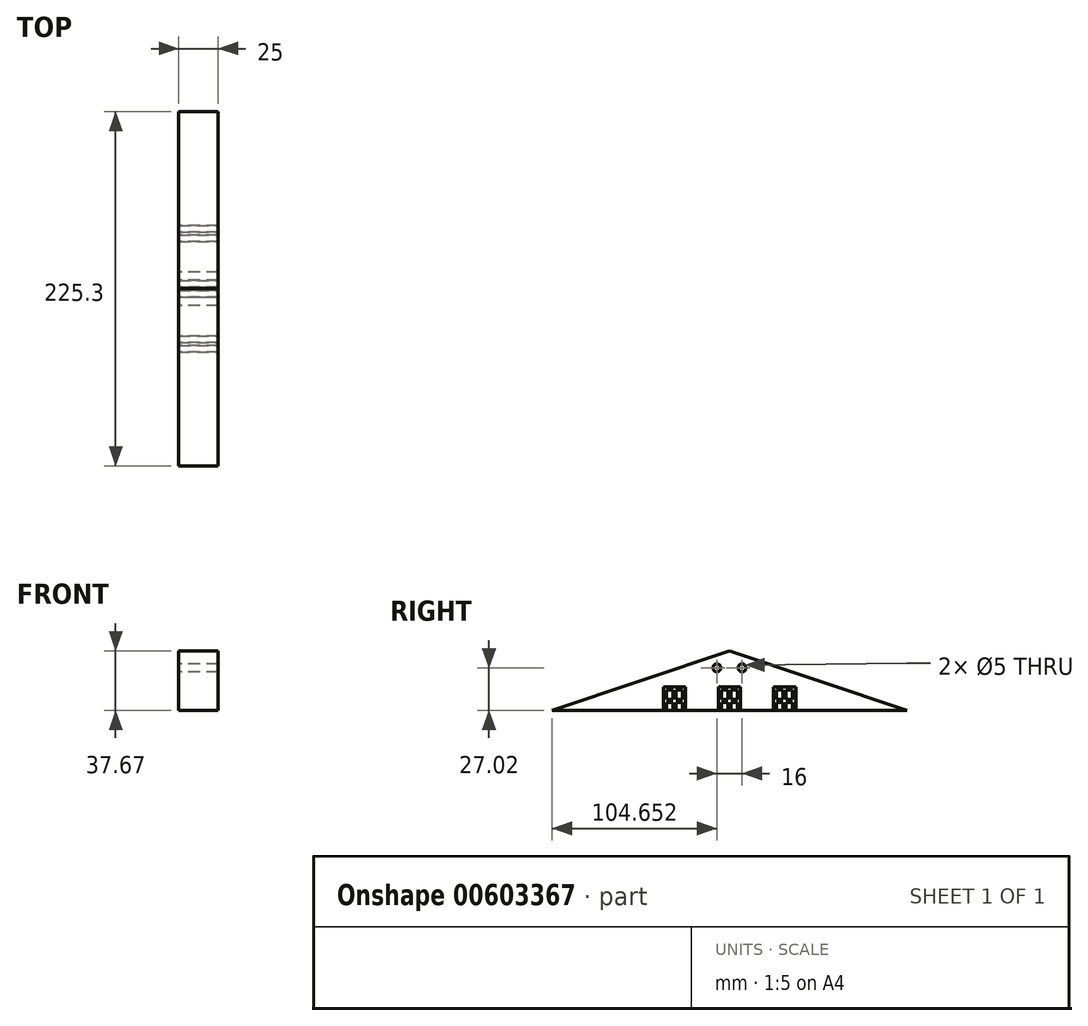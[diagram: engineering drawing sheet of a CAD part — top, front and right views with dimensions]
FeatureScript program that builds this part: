
annotation { "Feature Type Name" : "Feature", "Feature Type Description" : "" }
export const myFeature = defineFeature(function(context is Context, id is Id, definition is map)
    precondition{}
    {
        {
            var Q0;
            Q0=qCreatedBy(makeId("Top.planeOp"),FACE);
            var sketch = newSketch(context, id + "F0", { "sketchPlane" : qUnion([Q0])});
            skLineSegment(sketch, "E0", {"start": v(-327.3, -140.86) * mm, "end": v(-102.6, -140.86) * mm});
            skLineSegment(sketch, "E1", {"start": v(-102.6, -140.86) * mm, "end": v(-102.6, -170.86) * mm});
            skLineSegment(sketch, "E2", {"start": v(-102.6, -170.86) * mm, "end": v(0, -170.86) * mm});
            skLineSegment(sketch, "E3", {"start": v(0, -170.86) * mm, "end": v(0, -140.86) * mm});
            skLineSegment(sketch, "E4", {"start": v(0, -140.86) * mm, "end": v(288.9, -140.86) * mm});
            skLineSegment(sketch, "E5", {"start": v(288.9, -140.86) * mm, "end": v(288.9, 108.14) * mm});
            skLineSegment(sketch, "E6", {"start": v(288.9, 108.14) * mm, "end": v(0, 108.14) * mm});
            skLineSegment(sketch, "E7", {"start": v(0, 108.14) * mm, "end": v(0, 138.14) * mm});
            skLineSegment(sketch, "E8", {"start": v(-102.6, 128.64) * mm, "end": v(-102.6, 108.14) * mm});
            skLineSegment(sketch, "E9", {"start": v(-102.6, 108.14) * mm, "end": v(-327.3, 108.14) * mm});
            skLineSegment(sketch, "E10", {"start": v(-327.3, 108.14) * mm, "end": v(-327.3, -140.86) * mm});
            skLineSegment(sketch, "E11", {"start": v(-102.6, 128.64) * mm, "end": v(0, 138.14) * mm});
            skSolve(sketch);
        }
        {
            var Q0;
            Q0=makeQuery(id+"F0.imprint","IMPRINT",FACE,{"disambiguationData":[TD([[makeQuery(id+"F0.imprint","IMPRINT",EDGE,{"derivedFrom":sQuery(id+"F0.wireOp",EDGE,"E0")}),1.0]])]});
            extrude(context, id + "F1", {"entities" : qUnion([Q0]), "depth" : 8 * mm, "offsetDistance" : 25 * mm});
        }
        {
            var Q0;
            Q0=makeQuery(id+"F1.opExtrude","SWEPT_FACE",FACE,{"disambiguationData":[OSD([sQuery(id+"F0.wireOp",EDGE,"E5")])]});
            var sketch = newSketch(context, id + "F2", { "sketchPlane" : qUnion([Q0])});
            skLineSegment(sketch, "E12", {"start": v(-146.36, 8) * mm, "end": v(113.64, 8) * mm});
            skPoint(sketch, "E13", {"position": v(-140.86, 8) * mm});
            skPoint(sketch, "E14", {"position": v(108.14, 8) * mm});
            skLineSegment(sketch, "E15", {"start": v(-146.36, 8) * mm, "end": v(-16.36, 51.45) * mm});
            skLineSegment(sketch, "E16", {"start": v(-16.36, 51.45) * mm, "end": v(113.64, 8) * mm});
            skPoint(sketch, "E17", {"position": v(-16.36, 8) * mm});
            skSolve(sketch);
        }
        {
            var Q0;
            {var subQ0=sQuery(id+"F2.wireOp",EDGE,"E15");Q0=makeQuery(id+"F2.imprint","IMPRINT",FACE,{"disambiguationData":[TD([[makeQuery(id+"F2.imprint","IMPRINT",EDGE,{"derivedFrom":subQ0}),-1.0]])]});}
            extrude(context, id + "F3", {"entities" : qUnion([Q0]), "operationType" : NewBodyOperationType.ADD, "oppositeDirection" : true, "depth" : (616.2 + 5.5) * mm, "offsetDistance" : 25 * mm});
        }
        {
            var Q0;
            Q0=qSketchRegion(id+"F2",true);
            extrude(context, id + "F4", {"entities" : qUnion([Q0]), "operationType" : NewBodyOperationType.ADD, "depth" : 5.5 * mm, "offsetDistance" : 25 * mm});
        }
        {
            var Q0;
            Q0=makeQuery(id+"F1.opExtrude","SWEPT_FACE",FACE,{"disambiguationData":[OSD([sQuery(id+"F0.wireOp",EDGE,"E2")])]});
            var sketch = newSketch(context, id + "F5", { "sketchPlane" : qUnion([Q0])});
            skLineSegment(sketch, "E18", {"start": v(-108.1, 8) * mm, "end": v(5.5, 8) * mm});
            skPoint(sketch, "E19", {"position": v(-102.6, 8) * mm});
            skPoint(sketch, "E20", {"position": v(0, 8) * mm});
            skPoint(sketch, "E21", {"position": v(-51.3, 8) * mm});
            skLineSegment(sketch, "E22", {"start": v(-51.3, 8) * mm, "end": v(-51.3, 90.85) * mm, "construction": true});
            skPoint(sketch, "E23", {"position": v(-51.3, 62.75) * mm});
            skLineSegment(sketch, "E24", {"start": v(-108.1, 8) * mm, "end": v(-51.3, 62.75) * mm});
            skLineSegment(sketch, "E25", {"start": v(-51.3, 62.75) * mm, "end": v(5.5, 8) * mm});
            skSolve(sketch);
        }
        {
            var Q0;
            Q0=qSketchRegion(id+"F5",true);
            var Q1;
            Q1=makeQuery(id+"F1.opExtrude","SWEPT_FACE",FACE,{"disambiguationData":[OSD([sQuery(id+"F0.wireOp",EDGE,"E11")])]});
            extrude(context, id + "F6", {"entities" : qUnion([Q0]), "operationType" : NewBodyOperationType.ADD, "endBound" : BoundingType.UP_TO_SURFACE, "oppositeDirection" : true, "depth" : 25 * mm, "endBoundEntityFace" : qUnion([Q1]), "hasOffset" : true, "offsetDistance" : -5.5 * mm});
        }
        {
            var Q0;
            Q0=qSketchRegion(id+"F5",true);
            extrude(context, id + "F7", {"entities" : qUnion([Q0]), "operationType" : NewBodyOperationType.ADD, "depth" : 5.5 * mm, "offsetDistance" : 25 * mm});
        }
        {
            var Q0;
            Q0=makeQuery(id+"F6.opExtrude","CAP_FACE",FACE,{"disambiguationData":[OSD([sQuery(id+"F5.wireOp",EDGE,"E18"),sQuery(id+"F5.wireOp",EDGE,"E24"),sQuery(id+"F5.wireOp",EDGE,"E25")])],"isStart":false});
            var sketch = newSketch(context, id + "F8", { "sketchPlane" : qUnion([Q0])});
            skLineSegment(sketch, "E26.0", {"start": v(38.28, 55.82) * mm, "end": v(-15.3, 4.4) * mm});
            skLineSegment(sketch, "E26.1", {"start": v(91.86, 4.4) * mm, "end": v(38.28, 55.82) * mm});
            skLineSegment(sketch, "E27", {"start": v(-15.3, 4.4) * mm, "end": v(91.86, 4.4) * mm});
            skSolve(sketch);
        }
        {
            var Q0;
            {var subQ0=sQuery(id+"F8.wireOp",EDGE,"E26.1");var subQ1=sQuery(id+"F8.wireOp",EDGE,"E26.0");var subQ2=makeQuery(id+"F8.imprint","INTERSECT",VERTEX,{"derivedFrom":[subQ1,subQ0]});Q0=makeQuery(id+"F8.imprint","IMPRINT",FACE,{"disambiguationData":[TD([[makeQuery(id+"F8.imprint","IMPRINT",EDGE,{"disambiguationData":[TD([[subQ2,-1.0]])],"derivedFrom":subQ1}),1.0]])]});}
            extrude(context, id + "F9", {"entities" : qUnion([Q0]), "operationType" : NewBodyOperationType.REMOVE, "oppositeDirection" : true, "depth" : 5.5 * mm, "offsetDistance" : 25 * mm});
        }
        {
            var Q0;
            Q0=makeQuery(id+"F3.opExtrude","CAP_FACE",FACE,{"disambiguationData":[OSD([sQuery(id+"F2.wireOp",EDGE,"E12"),sQuery(id+"F2.wireOp",EDGE,"E15"),sQuery(id+"F2.wireOp",EDGE,"E16")])],"isStart":false});
            var sketch = newSketch(context, id + "F10", { "sketchPlane" : qUnion([Q0])});
            skLineSegment(sketch, "E28.0", {"start": v(16.36, 45.65) * mm, "end": v(-111.9, 2.78) * mm});
            skLineSegment(sketch, "E28.1", {"start": v(144.61, 2.78) * mm, "end": v(16.36, 45.65) * mm});
            skLineSegment(sketch, "E29", {"start": v(-111.9, 2.78) * mm, "end": v(144.61, 2.78) * mm});
            skSolve(sketch);
        }
        {
            var Q0;
            Q0=qSketchRegion(id+"F10",true);
            extrude(context, id + "F11", {"entities" : qUnion([Q0]), "operationType" : NewBodyOperationType.REMOVE, "oppositeDirection" : true, "depth" : 5.5 * mm, "offsetDistance" : 25 * mm});
        }
        {
            var Q0;
            Q0=makeQuery(id+"F4.opExtrude","CAP_FACE",FACE,{"disambiguationData":[OSD([sQuery(id+"F2.wireOp",EDGE,"E12"),sQuery(id+"F2.wireOp",EDGE,"E15"),sQuery(id+"F2.wireOp",EDGE,"E16")])],"isStart":false});
            var sketch = newSketch(context, id + "F12", { "sketchPlane" : qUnion([Q0])});
            skLineSegment(sketch, "E30.0", {"start": v(-16.36, 45.65) * mm, "end": v(111.9, 2.78) * mm});
            skLineSegment(sketch, "E30.1", {"start": v(-144.61, 2.78) * mm, "end": v(-16.36, 45.65) * mm});
            skLineSegment(sketch, "E31", {"start": v(-144.61, 2.78) * mm, "end": v(111.9, 2.78) * mm});
            skSolve(sketch);
        }
        {
            var Q0;
            Q0=qSketchRegion(id+"F12",true);
            extrude(context, id + "F13", {"entities" : qUnion([Q0]), "operationType" : NewBodyOperationType.REMOVE, "oppositeDirection" : true, "depth" : 5.5 * mm, "offsetDistance" : 25 * mm});
        }
        {
            var Q0;
            Q0=makeQuery(id+"F7.opExtrude","CAP_FACE",FACE,{"disambiguationData":[OSD([sQuery(id+"F5.wireOp",EDGE,"E18"),sQuery(id+"F5.wireOp",EDGE,"E24"),sQuery(id+"F5.wireOp",EDGE,"E25")])],"isStart":false});
            var sketch = newSketch(context, id + "F14", { "sketchPlane" : qUnion([Q0])});
            skLineSegment(sketch, "E32.0", {"start": v(-51.3, 55.11) * mm, "end": v(1.68, 4.04) * mm});
            skLineSegment(sketch, "E32.1", {"start": v(-104.28, 4.04) * mm, "end": v(-51.3, 55.11) * mm});
            skLineSegment(sketch, "E33", {"start": v(-104.28, 4.04) * mm, "end": v(1.68, 4.04) * mm});
            skSolve(sketch);
        }
        {
            var Q0;
            Q0=qSketchRegion(id+"F14",true);
            extrude(context, id + "F15", {"entities" : qUnion([Q0]), "operationType" : NewBodyOperationType.REMOVE, "oppositeDirection" : true, "depth" : 5.5 * mm, "offsetDistance" : 25 * mm});
        }
        {
            var Q0;
            Q0=makeQuery(id+"F4.opExtrude","CAP_FACE",FACE,{"disambiguationData":[OSD([sQuery(id+"F2.wireOp",EDGE,"E12"),sQuery(id+"F2.wireOp",EDGE,"E15"),sQuery(id+"F2.wireOp",EDGE,"E16")])],"isStart":false});
            var sketch = newSketch(context, id + "F16", { "sketchPlane" : qUnion([Q0])});
            skLineSegment(sketch, "E34", {"start": v(-36.64, 44.67) * mm, "end": v(-16.36, 51.45) * mm});
            skLineSegment(sketch, "E35", {"start": v(-16.36, 51.45) * mm, "end": v(3.93, 44.67) * mm});
            skLineSegment(sketch, "E36.0", {"start": v(-16.36, 55.67) * mm, "end": v(5.2, 48.47) * mm});
            skLineSegment(sketch, "E36.1", {"start": v(-37.91, 48.47) * mm, "end": v(-16.36, 55.67) * mm});
            skLineSegment(sketch, "E37", {"start": v(-37.91, 48.47) * mm, "end": v(-36.64, 44.67) * mm});
            skLineSegment(sketch, "E38", {"start": v(5.2, 48.47) * mm, "end": v(3.93, 44.67) * mm});
            skSolve(sketch);
        }
        {
            var Q0;
            Q0=makeQuery(id+"F16.imprint","IMPRINT",FACE,{"disambiguationData":[TD([[makeQuery(id+"F16.imprint","IMPRINT",EDGE,{"derivedFrom":sQuery(id+"F16.wireOp",EDGE,"E34")}),1.0]])]});
            extrude(context, id + "F17", {"entities" : qUnion([Q0]), "operationType" : NewBodyOperationType.ADD, "oppositeDirection" : true, "depth" : (30.35 + 277.85) * mm, "offsetDistance" : 25 * mm});
        }
        {
            var Q0;
            Q0=qSketchRegion(id+"F16",true);
            extrude(context, id + "F18", {"entities" : qUnion([Q0]), "operationType" : NewBodyOperationType.REMOVE, "oppositeDirection" : true, "depth" : 24 * mm, "offsetDistance" : 25 * mm});
        }
        {
            var Q0;
            Q0=makeQuery(id+"F3.opExtrude","CAP_FACE",FACE,{"disambiguationData":[OSD([sQuery(id+"F2.wireOp",EDGE,"E12"),sQuery(id+"F2.wireOp",EDGE,"E15"),sQuery(id+"F2.wireOp",EDGE,"E16")])],"isStart":false});
            var sketch = newSketch(context, id + "F19", { "sketchPlane" : qUnion([Q0])});
            skLineSegment(sketch, "E39", {"start": v(-3.93, 44.67) * mm, "end": v(16.36, 51.45) * mm});
            skLineSegment(sketch, "E40", {"start": v(16.36, 51.45) * mm, "end": v(36.64, 44.67) * mm});
            skLineSegment(sketch, "E41.0", {"start": v(16.36, 55.67) * mm, "end": v(37.91, 48.47) * mm});
            skLineSegment(sketch, "E41.1", {"start": v(-5.2, 48.47) * mm, "end": v(16.36, 55.67) * mm});
            skLineSegment(sketch, "E42", {"start": v(-5.2, 48.47) * mm, "end": v(-3.93, 44.67) * mm});
            skLineSegment(sketch, "E43", {"start": v(37.91, 48.47) * mm, "end": v(36.64, 44.67) * mm});
            skSolve(sketch);
        }
        {
            var Q0;
            Q0=qSketchRegion(id+"F19",true);
            extrude(context, id + "F20", {"entities" : qUnion([Q0]), "operationType" : NewBodyOperationType.ADD, "oppositeDirection" : true, "depth" : (30.35 + 213.85) * mm, "offsetDistance" : 25 * mm});
        }
        {
            var Q0;
            Q0=qSketchRegion(id+"F19",true);
            extrude(context, id + "F21", {"entities" : qUnion([Q0]), "operationType" : NewBodyOperationType.REMOVE, "oppositeDirection" : true, "depth" : 30.35 * mm, "offsetDistance" : 25 * mm});
        }
        {
            var Q0;
            Q0=makeQuery(id+"F11.boolean.opBoolean","MERGE",FACE,{"derivedFrom":[makeQuery(id+"F1.opExtrude","SWEPT_FACE",FACE,{"disambiguationData":[OSD([sQuery(id+"F0.wireOp",EDGE,"E10")])]}),makeQuery(id+"F11.opExtrude","CAP_FACE",FACE,{"disambiguationData":[OSD([sQuery(id+"F10.wireOp",EDGE,"E28.0"),sQuery(id+"F10.wireOp",EDGE,"E28.1"),sQuery(id+"F10.wireOp",EDGE,"E29")])],"isStart":false})]});
            var sketch = newSketch(context, id + "F22", { "sketchPlane" : qUnion([Q0])});
            skPoint(sketch, "E44", {"position": v(16.36, 0) * mm});
            skLineSegment(sketch, "E45", {"start": v(16.36, 0) * mm, "end": v(16.36, 35) * mm, "construction": true});
            skLineSegment(sketch, "E46", {"start": v(-4.2, 35) * mm, "end": v(35.76, 35) * mm, "construction": true});
            skPoint(sketch, "E47", {"position": v(8.36, 35) * mm});
            skPoint(sketch, "E48", {"position": v(24.36, 35) * mm});
            skCircle(sketch, "E49", {"center": v(8.36, 35) * mm, "radius": 2.5 * mm});
            skCircle(sketch, "E50", {"center": v(24.36, 35) * mm, "radius": 2.5 * mm});
            skSolve(sketch);
        }
        {
            var Q0;
            Q0=qSketchRegion(id+"F22",true);
            extrude(context, id + "F23", {"entities" : qUnion([Q0]), "operationType" : NewBodyOperationType.REMOVE, "oppositeDirection" : true, "depth" : .5 * mm, "offsetDistance" : 25 * mm});
        }
        {
            var Q0;
            Q0=makeQuery(id+"F13.boolean.opBoolean","MERGE",FACE,{"derivedFrom":[makeQuery(id+"F3.boolean.opBoolean","MERGE",FACE,{"derivedFrom":[makeQuery(id+"F1.opExtrude","SWEPT_FACE",FACE,{"disambiguationData":[OSD([sQuery(id+"F0.wireOp",EDGE,"E5")])]}),makeQuery(id+"F3.opExtrude","CAP_FACE",FACE,{"disambiguationData":[OSD([sQuery(id+"F2.wireOp",EDGE,"E12"),sQuery(id+"F2.wireOp",EDGE,"E15"),sQuery(id+"F2.wireOp",EDGE,"E16")])],"isStart":true})]}),makeQuery(id+"F13.opExtrude","CAP_FACE",FACE,{"disambiguationData":[OSD([sQuery(id+"F12.wireOp",EDGE,"E30.0"),sQuery(id+"F12.wireOp",EDGE,"E30.1"),sQuery(id+"F12.wireOp",EDGE,"E31")])],"isStart":false})]});
            var sketch = newSketch(context, id + "F24", { "sketchPlane" : qUnion([Q0])});
            skPoint(sketch, "E51", {"position": v(-16.36, 0) * mm});
            skLineSegment(sketch, "E52", {"start": v(-16.36, 0) * mm, "end": v(-16.36, 35) * mm, "construction": true});
            skLineSegment(sketch, "E53", {"start": v(-48.45, 35) * mm, "end": v(-8.49, 35) * mm, "construction": true});
            skPoint(sketch, "E54", {"position": v(-24.36, 35) * mm});
            skPoint(sketch, "E55", {"position": v(-8.36, 35) * mm});
            skCircle(sketch, "E56", {"center": v(-24.36, 35) * mm, "radius": 2.5 * mm});
            skCircle(sketch, "E57", {"center": v(-8.36, 35) * mm, "radius": 2.5 * mm});
            skSolve(sketch);
        }
        {
            var Q0;
            Q0=qSketchRegion(id+"F24",true);
            extrude(context, id + "F25", {"entities" : qUnion([Q0]), "operationType" : NewBodyOperationType.REMOVE, "oppositeDirection" : true, "depth" : .5 * mm, "offsetDistance" : 25 * mm});
        }
        {
            var Q0;
            Q0=makeQuery(id+"F15.boolean.opBoolean","MERGE",FACE,{"derivedFrom":[makeQuery(id+"F6.boolean.opBoolean","MERGE",FACE,{"derivedFrom":[makeQuery(id+"F1.opExtrude","SWEPT_FACE",FACE,{"disambiguationData":[OSD([sQuery(id+"F0.wireOp",EDGE,"E2")])]}),makeQuery(id+"F6.opExtrude","CAP_FACE",FACE,{"disambiguationData":[OSD([sQuery(id+"F5.wireOp",EDGE,"E18"),sQuery(id+"F5.wireOp",EDGE,"E24"),sQuery(id+"F5.wireOp",EDGE,"E25")])],"isStart":true})]})],"fromTools":[makeQuery(id+"F15.opExtrude","CAP_FACE",FACE,{"disambiguationData":[OSD([sQuery(id+"F14.wireOp",EDGE,"E32.0"),sQuery(id+"F14.wireOp",EDGE,"E32.1"),sQuery(id+"F14.wireOp",EDGE,"E33")])],"isStart":false})]});
            var sketch = newSketch(context, id + "F26", { "sketchPlane" : qUnion([Q0])});
            skPoint(sketch, "E58", {"position": v(-51.3, 0) * mm});
            skLineSegment(sketch, "E59", {"start": v(-51.3, 0) * mm, "end": v(-51.3, 35) * mm, "construction": true});
            skLineSegment(sketch, "E60", {"start": v(-73.66, 35) * mm, "end": v(-33.7, 35) * mm, "construction": true});
            skPoint(sketch, "E61", {"position": v(-59.3, 35) * mm});
            skPoint(sketch, "E62", {"position": v(-43.3, 35) * mm});
            skCircle(sketch, "E63", {"center": v(-59.3, 35) * mm, "radius": 2.5 * mm});
            skCircle(sketch, "E64", {"center": v(-43.3, 35) * mm, "radius": 2.5 * mm});
            skSolve(sketch);
        }
        {
            var Q0;
            Q0=qSketchRegion(id+"F26",true);
            extrude(context, id + "F27", {"entities" : qUnion([Q0]), "operationType" : NewBodyOperationType.REMOVE, "oppositeDirection" : true, "depth" : .5 * mm, "offsetDistance" : 25 * mm});
        }
        {
            var Q0;
            Q0=makeQuery(id+"F1.opExtrude","SWEPT_FACE",FACE,{"disambiguationData":[OSD([sQuery(id+"F0.wireOp",EDGE,"E11")])]});
            var sketch = newSketch(context, id + "F28", { "sketchPlane" : qUnion([Q0])});
            skPoint(sketch, "E65", {"position": v(38.78, 0) * mm});
            skLineSegment(sketch, "E66", {"start": v(38.78, 0) * mm, "end": v(38.78, 35) * mm, "construction": true});
            skLineSegment(sketch, "E67", {"start": v(13.04, 35) * mm, "end": v(53, 35) * mm, "construction": true});
            skPoint(sketch, "E68", {"position": v(30.78, 35) * mm});
            skPoint(sketch, "E69", {"position": v(46.78, 35) * mm});
            skCircle(sketch, "E70", {"center": v(30.78, 35) * mm, "radius": 2.5 * mm});
            skCircle(sketch, "E71", {"center": v(46.78, 35) * mm, "radius": 2.5 * mm});
            skSolve(sketch);
        }
        {
            var Q0;
            Q0=qSketchRegion(id+"F28",true);
            extrude(context, id + "F29", {"entities" : qUnion([Q0]), "operationType" : NewBodyOperationType.REMOVE, "oppositeDirection" : true, "depth" : .5 * mm, "offsetDistance" : 25 * mm});
        }
        {
            var Q0;
            Q0=makeQuery(id+"F13.boolean.opBoolean","MERGE",FACE,{"derivedFrom":[makeQuery(id+"F3.boolean.opBoolean","MERGE",FACE,{"derivedFrom":[makeQuery(id+"F1.opExtrude","SWEPT_FACE",FACE,{"disambiguationData":[OSD([sQuery(id+"F0.wireOp",EDGE,"E5")])]}),makeQuery(id+"F3.opExtrude","CAP_FACE",FACE,{"disambiguationData":[OSD([sQuery(id+"F2.wireOp",EDGE,"E12"),sQuery(id+"F2.wireOp",EDGE,"E15"),sQuery(id+"F2.wireOp",EDGE,"E16")])],"isStart":true})]}),makeQuery(id+"F13.opExtrude","CAP_FACE",FACE,{"disambiguationData":[OSD([sQuery(id+"F12.wireOp",EDGE,"E30.0"),sQuery(id+"F12.wireOp",EDGE,"E30.1"),sQuery(id+"F12.wireOp",EDGE,"E31")])],"isStart":false})]});
            var sketch = newSketch(context, id + "F30", { "sketchPlane" : qUnion([Q0])});
            skPoint(sketch, "E72", {"position": v(-16.36, 0) * mm});
            skLineSegment(sketch, "E73", {"start": v(-16.36, 0) * mm, "end": v(-16.36, 40.85) * mm, "construction": true});
            skLineSegment(sketch, "E74.bottom", {"start": v(-23.43, 23) * mm, "end": v(-9.29, 23) * mm});
            skLineSegment(sketch, "E74.top", {"start": v(-23.43, 5) * mm, "end": v(-9.29, 5) * mm});
            skLineSegment(sketch, "E74.left", {"start": v(-23.43, 23) * mm, "end": v(-23.43, 5) * mm});
            skLineSegment(sketch, "E74.right", {"start": v(-9.29, 23) * mm, "end": v(-9.29, 5) * mm});
            skLineSegment(sketch, "E75.0", {"start": v(-21.5, 21.07) * mm, "end": v(-17.32, 21.07) * mm});
            skLineSegment(sketch, "E75.1", {"start": v(-21.5, 21.07) * mm, "end": v(-21.5, 14.96) * mm});
            skLineSegment(sketch, "E75.2", {"start": v(-21.5, 6.93) * mm, "end": v(-17.32, 6.93) * mm});
            skLineSegment(sketch, "E75.3", {"start": v(-11.21, 21.07) * mm, "end": v(-11.21, 14.96) * mm});
            skLineSegment(sketch, "E76.left", {"start": v(-17.32, 21.07) * mm, "end": v(-17.32, 14.96) * mm});
            skLineSegment(sketch, "E76.right", {"start": v(-15.4, 21.07) * mm, "end": v(-15.4, 14.96) * mm});
            skLineSegment(sketch, "E77.bottom", {"start": v(-11.21, 14.96) * mm, "end": v(-15.4, 14.96) * mm});
            skLineSegment(sketch, "E77.top", {"start": v(-11.21, 13.04) * mm, "end": v(-15.4, 13.04) * mm});
            skLineSegment(sketch, "E78.trimOffspring", {"start": v(-17.32, 14.96) * mm, "end": v(-21.5, 14.96) * mm});
            skLineSegment(sketch, "E79.trimOffspring", {"start": v(-17.32, 13.04) * mm, "end": v(-17.32, 6.93) * mm});
            skLineSegment(sketch, "E80.trimOffspring", {"start": v(-17.32, 13.04) * mm, "end": v(-21.5, 13.04) * mm});
            skLineSegment(sketch, "E81.trimOffspring", {"start": v(-15.4, 13.04) * mm, "end": v(-15.4, 6.93) * mm});
            skLineSegment(sketch, "E82.trimOffspring", {"start": v(-11.21, 13.04) * mm, "end": v(-11.21, 6.93) * mm});
            skLineSegment(sketch, "E83.trimOffspring", {"start": v(-21.5, 13.04) * mm, "end": v(-21.5, 6.93) * mm});
            skLineSegment(sketch, "E84.trimOffspring", {"start": v(-15.4, 21.07) * mm, "end": v(-11.21, 21.07) * mm});
            skLineSegment(sketch, "E85.trimOffspring", {"start": v(-15.4, 6.93) * mm, "end": v(-11.21, 6.93) * mm});
            skPoint(sketch, "E86", {"position": v(-16.36, 23) * mm});
            skLineSegment(sketch, "E87.1.0.0", {"start": v(19.6, 13.04) * mm, "end": v(19.6, 6.93) * mm});
            skPoint(sketch, "E87.1.0.1", {"position": v(18.64, 23) * mm});
            skLineSegment(sketch, "E87.1.0.2", {"start": v(19.6, 6.93) * mm, "end": v(23.79, 6.93) * mm});
            skLineSegment(sketch, "E87.1.0.3", {"start": v(13.5, 13.04) * mm, "end": v(13.5, 6.93) * mm});
            skLineSegment(sketch, "E87.1.0.4", {"start": v(17.68, 13.04) * mm, "end": v(17.68, 6.93) * mm});
            skLineSegment(sketch, "E87.1.0.5", {"start": v(11.57, 5) * mm, "end": v(25.71, 5) * mm});
            skLineSegment(sketch, "E87.1.0.6", {"start": v(11.57, 23) * mm, "end": v(25.71, 23) * mm});
            skLineSegment(sketch, "E87.1.0.7", {"start": v(25.71, 23) * mm, "end": v(25.71, 5) * mm});
            skLineSegment(sketch, "E87.1.0.8", {"start": v(11.57, 23) * mm, "end": v(11.57, 5) * mm});
            skLineSegment(sketch, "E87.1.0.9", {"start": v(23.79, 13.04) * mm, "end": v(23.79, 6.93) * mm});
            skLineSegment(sketch, "E87.1.0.10", {"start": v(23.79, 13.04) * mm, "end": v(19.6, 13.04) * mm});
            skLineSegment(sketch, "E87.1.0.11", {"start": v(17.68, 21.07) * mm, "end": v(17.68, 14.96) * mm});
            skLineSegment(sketch, "E87.1.0.12", {"start": v(13.5, 21.07) * mm, "end": v(17.68, 21.07) * mm});
            skLineSegment(sketch, "E87.1.0.13", {"start": v(19.6, 21.07) * mm, "end": v(19.6, 14.96) * mm});
            skLineSegment(sketch, "E87.1.0.14", {"start": v(13.5, 6.93) * mm, "end": v(17.68, 6.93) * mm});
            skLineSegment(sketch, "E87.1.0.15", {"start": v(23.79, 21.07) * mm, "end": v(23.79, 14.96) * mm});
            skLineSegment(sketch, "E87.1.0.16", {"start": v(17.68, 13.04) * mm, "end": v(13.5, 13.04) * mm});
            skLineSegment(sketch, "E87.1.0.17", {"start": v(17.68, 14.96) * mm, "end": v(13.5, 14.96) * mm});
            skLineSegment(sketch, "E87.1.0.18", {"start": v(23.79, 14.96) * mm, "end": v(19.6, 14.96) * mm});
            skLineSegment(sketch, "E87.1.0.19", {"start": v(19.6, 21.07) * mm, "end": v(23.79, 21.07) * mm});
            skLineSegment(sketch, "E87.1.0.20", {"start": v(13.5, 21.07) * mm, "end": v(13.5, 14.96) * mm});
            skLineSegment(sketch, "E87.direction1", {"start": v(-23.43, 5) * mm, "end": v(11.57, 5) * mm, "construction": true});
            skLineSegment(sketch, "E88.1.0.0", {"start": v(-50.4, 6.93) * mm, "end": v(-46.21, 6.93) * mm});
            skPoint(sketch, "E88.1.0.1", {"position": v(-51.36, 0) * mm});
            skLineSegment(sketch, "E88.1.0.2", {"start": v(-58.43, 5) * mm, "end": v(-44.29, 5) * mm});
            skLineSegment(sketch, "E88.1.0.3", {"start": v(-44.29, 23) * mm, "end": v(-44.29, 5) * mm});
            skLineSegment(sketch, "E88.1.0.4", {"start": v(-58.43, 23) * mm, "end": v(-58.43, 5) * mm});
            skLineSegment(sketch, "E88.1.0.5", {"start": v(-46.21, 21.07) * mm, "end": v(-46.21, 14.96) * mm});
            skLineSegment(sketch, "E88.1.0.6", {"start": v(-56.5, 6.93) * mm, "end": v(-52.32, 6.93) * mm});
            skPoint(sketch, "E88.1.0.7", {"position": v(-51.36, 23) * mm});
            skLineSegment(sketch, "E88.1.0.8", {"start": v(-50.4, 13.04) * mm, "end": v(-50.4, 6.93) * mm});
            skLineSegment(sketch, "E88.1.0.9", {"start": v(-52.32, 13.04) * mm, "end": v(-56.5, 13.04) * mm});
            skLineSegment(sketch, "E88.1.0.10", {"start": v(-52.32, 13.04) * mm, "end": v(-52.32, 6.93) * mm});
            skLineSegment(sketch, "E88.1.0.11", {"start": v(-58.43, 23) * mm, "end": v(-44.29, 23) * mm});
            skLineSegment(sketch, "E88.1.0.12", {"start": v(-52.32, 14.96) * mm, "end": v(-56.5, 14.96) * mm});
            skLineSegment(sketch, "E88.1.0.13", {"start": v(-46.21, 13.04) * mm, "end": v(-50.4, 13.04) * mm});
            skLineSegment(sketch, "E88.1.0.14", {"start": v(-46.21, 14.96) * mm, "end": v(-50.4, 14.96) * mm});
            skLineSegment(sketch, "E88.1.0.15", {"start": v(-50.4, 21.07) * mm, "end": v(-46.21, 21.07) * mm});
            skLineSegment(sketch, "E88.1.0.16", {"start": v(-56.5, 21.07) * mm, "end": v(-56.5, 14.96) * mm});
            skLineSegment(sketch, "E88.1.0.17", {"start": v(-56.5, 21.07) * mm, "end": v(-52.32, 21.07) * mm});
            skLineSegment(sketch, "E88.1.0.18", {"start": v(-50.4, 21.07) * mm, "end": v(-50.4, 14.96) * mm});
            skLineSegment(sketch, "E88.1.0.19", {"start": v(-52.32, 21.07) * mm, "end": v(-52.32, 14.96) * mm});
            skLineSegment(sketch, "E88.1.0.20", {"start": v(-56.5, 13.04) * mm, "end": v(-56.5, 6.93) * mm});
            skLineSegment(sketch, "E88.1.0.21", {"start": v(-46.21, 13.04) * mm, "end": v(-46.21, 6.93) * mm});
            skLineSegment(sketch, "E88.direction1", {"start": v(-23.43, 5) * mm, "end": v(-58.43, 5) * mm, "construction": true});
            skSolve(sketch);
        }
        {
            var Q0;
            Q0=qSketchRegion(id+"F30",true);
            extrude(context, id + "F31", {"entities" : qUnion([Q0]), "operationType" : NewBodyOperationType.REMOVE, "oppositeDirection" : true, "depth" : 0.5 * mm, "offsetDistance" : 25 * mm});
        }
        {
            var Q0;
            {var subQ1=sQuery(id+"F0.wireOp",EDGE,"E5");var subQ2=sQuery(id+"F0.wireOp",EDGE,"E4");var subQ3=sQuery(id+"F2.wireOp",EDGE,"E12");var subQ4=sQuery(id+"F12.wireOp",EDGE,"E30.0");var subQ6=sQuery(id+"F12.wireOp",EDGE,"E30.1");Q0=makeQuery(id+"F31.boolean.opBoolean","SPLIT",FACE,{"disambiguationData":[TD([makeQuery(id+"F1.opExtrude","SWEPT_FACE",FACE,{"disambiguationData":[OSD([subQ2])]})])],"derivedFrom":makeQuery(id+"F13.boolean.opBoolean","MERGE",FACE,{"derivedFrom":[makeQuery(id+"F3.boolean.opBoolean","MERGE",FACE,{"derivedFrom":[makeQuery(id+"F1.opExtrude","SWEPT_FACE",FACE,{"disambiguationData":[OSD([subQ1])]}),makeQuery(id+"F3.opExtrude","CAP_FACE",FACE,{"disambiguationData":[OSD([subQ3,sQuery(id+"F2.wireOp",EDGE,"E15"),sQuery(id+"F2.wireOp",EDGE,"E16")])],"isStart":true})]}),makeQuery(id+"F13.opExtrude","CAP_FACE",FACE,{"disambiguationData":[OSD([subQ4,subQ6,sQuery(id+"F12.wireOp",EDGE,"E31")])],"isStart":false})]})});}
            var Q1;
            Q1=makeQuery(id+"F31.boolean.opBoolean","COPY",FACE,{"derivedFrom":makeQuery(id+"F31.opExtrude","CAP_FACE",FACE,{"disambiguationData":[OSD([sQuery(id+"F30.wireOp",EDGE,"E88.1.0.0"),sQuery(id+"F30.wireOp",EDGE,"E88.1.0.2"),sQuery(id+"F30.wireOp",EDGE,"E88.1.0.3"),sQuery(id+"F30.wireOp",EDGE,"E88.1.0.4"),sQuery(id+"F30.wireOp",EDGE,"E88.1.0.5"),sQuery(id+"F30.wireOp",EDGE,"E88.1.0.6"),sQuery(id+"F30.wireOp",EDGE,"E88.1.0.8"),sQuery(id+"F30.wireOp",EDGE,"E88.1.0.9"),sQuery(id+"F30.wireOp",EDGE,"E88.1.0.10"),sQuery(id+"F30.wireOp",EDGE,"E88.1.0.11"),sQuery(id+"F30.wireOp",EDGE,"E88.1.0.12"),sQuery(id+"F30.wireOp",EDGE,"E88.1.0.13"),sQuery(id+"F30.wireOp",EDGE,"E88.1.0.14"),sQuery(id+"F30.wireOp",EDGE,"E88.1.0.15"),sQuery(id+"F30.wireOp",EDGE,"E88.1.0.16"),sQuery(id+"F30.wireOp",EDGE,"E88.1.0.17"),sQuery(id+"F30.wireOp",EDGE,"E88.1.0.18"),sQuery(id+"F30.wireOp",EDGE,"E88.1.0.19"),sQuery(id+"F30.wireOp",EDGE,"E88.1.0.20"),sQuery(id+"F30.wireOp",EDGE,"E88.1.0.21")])],"isStart":false})});
            var Q2;
            Q2=makeQuery(id+"F31.boolean.opBoolean","COPY",FACE,{"derivedFrom":makeQuery(id+"F31.opExtrude","CAP_FACE",FACE,{"disambiguationData":[OSD([sQuery(id+"F30.wireOp",EDGE,"E74.bottom"),sQuery(id+"F30.wireOp",EDGE,"E74.top"),sQuery(id+"F30.wireOp",EDGE,"E74.left"),sQuery(id+"F30.wireOp",EDGE,"E74.right"),sQuery(id+"F30.wireOp",EDGE,"E75.0"),sQuery(id+"F30.wireOp",EDGE,"E75.1"),sQuery(id+"F30.wireOp",EDGE,"E75.2"),sQuery(id+"F30.wireOp",EDGE,"E75.3"),sQuery(id+"F30.wireOp",EDGE,"E76.left"),sQuery(id+"F30.wireOp",EDGE,"E76.right"),sQuery(id+"F30.wireOp",EDGE,"E77.bottom"),sQuery(id+"F30.wireOp",EDGE,"E77.top"),sQuery(id+"F30.wireOp",EDGE,"E78.trimOffspring"),sQuery(id+"F30.wireOp",EDGE,"E79.trimOffspring"),sQuery(id+"F30.wireOp",EDGE,"E80.trimOffspring"),sQuery(id+"F30.wireOp",EDGE,"E81.trimOffspring"),sQuery(id+"F30.wireOp",EDGE,"E82.trimOffspring"),sQuery(id+"F30.wireOp",EDGE,"E83.trimOffspring"),sQuery(id+"F30.wireOp",EDGE,"E84.trimOffspring"),sQuery(id+"F30.wireOp",EDGE,"E85.trimOffspring")])],"isStart":false})});
            var Q3;
            Q3=makeQuery(id+"F31.boolean.opBoolean","COPY",FACE,{"derivedFrom":makeQuery(id+"F31.opExtrude","CAP_FACE",FACE,{"disambiguationData":[OSD([sQuery(id+"F30.wireOp",EDGE,"E87.1.0.0"),sQuery(id+"F30.wireOp",EDGE,"E87.1.0.2"),sQuery(id+"F30.wireOp",EDGE,"E87.1.0.3"),sQuery(id+"F30.wireOp",EDGE,"E87.1.0.4"),sQuery(id+"F30.wireOp",EDGE,"E87.1.0.5"),sQuery(id+"F30.wireOp",EDGE,"E87.1.0.6"),sQuery(id+"F30.wireOp",EDGE,"E87.1.0.7"),sQuery(id+"F30.wireOp",EDGE,"E87.1.0.8"),sQuery(id+"F30.wireOp",EDGE,"E87.1.0.9"),sQuery(id+"F30.wireOp",EDGE,"E87.1.0.10"),sQuery(id+"F30.wireOp",EDGE,"E87.1.0.11"),sQuery(id+"F30.wireOp",EDGE,"E87.1.0.12"),sQuery(id+"F30.wireOp",EDGE,"E87.1.0.13"),sQuery(id+"F30.wireOp",EDGE,"E87.1.0.14"),sQuery(id+"F30.wireOp",EDGE,"E87.1.0.15"),sQuery(id+"F30.wireOp",EDGE,"E87.1.0.16"),sQuery(id+"F30.wireOp",EDGE,"E87.1.0.17"),sQuery(id+"F30.wireOp",EDGE,"E87.1.0.18"),sQuery(id+"F30.wireOp",EDGE,"E87.1.0.19"),sQuery(id+"F30.wireOp",EDGE,"E87.1.0.20")])],"isStart":false})});
            extrude(context, id + "F32", {"entities" : qUnion([Q0, Q1, Q2, Q3]), "depth" : 25 * mm, "offsetDistance" : 25 * mm});
        }
        {
            var Q0;
            Q0=makeQuery(id+"F1.opExtrude","SWEPT_BODY",BODY,{"disambiguationData":[OSD([sQuery(id+"F0.wireOp",EDGE,"E0"),sQuery(id+"F0.wireOp",EDGE,"E1"),sQuery(id+"F0.wireOp",EDGE,"E2"),sQuery(id+"F0.wireOp",EDGE,"E3"),sQuery(id+"F0.wireOp",EDGE,"E4"),sQuery(id+"F0.wireOp",EDGE,"E5"),sQuery(id+"F0.wireOp",EDGE,"E6"),sQuery(id+"F0.wireOp",EDGE,"E7"),sQuery(id+"F0.wireOp",EDGE,"E8"),sQuery(id+"F0.wireOp",EDGE,"E9"),sQuery(id+"F0.wireOp",EDGE,"E10"),sQuery(id+"F0.wireOp",EDGE,"E11")])]});
            deleteBodies(context, id + "F33", {"entities" : qUnion([Q0])});
        }
        {
            var Q0;
            Q0=makeQuery(id+"F32.opExtrude","SWEPT_FACE",FACE,{"disambiguationData":[OSD([sQuery(id+"F0.wireOp",EDGE,"E5")])]});
            extrude(context, id + "F34", {"entities" : qUnion([Q0]), "operationType" : NewBodyOperationType.REMOVE, "oppositeDirection" : true, "depth" : 8 * mm, "offsetDistance" : 25 * mm});
        }
        {
            var Q0;
            Q0=makeQuery(id+"F32.opExtrude","CAP_FACE",FACE,{"disambiguationData":[OSD([sQuery(id+"F30.wireOp",EDGE,"E87.1.0.0"),sQuery(id+"F30.wireOp",EDGE,"E87.1.0.2"),sQuery(id+"F30.wireOp",EDGE,"E87.1.0.3"),sQuery(id+"F30.wireOp",EDGE,"E87.1.0.4"),sQuery(id+"F30.wireOp",EDGE,"E87.1.0.5"),sQuery(id+"F30.wireOp",EDGE,"E87.1.0.6"),sQuery(id+"F30.wireOp",EDGE,"E87.1.0.7"),sQuery(id+"F30.wireOp",EDGE,"E87.1.0.8"),sQuery(id+"F30.wireOp",EDGE,"E87.1.0.9"),sQuery(id+"F30.wireOp",EDGE,"E87.1.0.10"),sQuery(id+"F30.wireOp",EDGE,"E87.1.0.11"),sQuery(id+"F30.wireOp",EDGE,"E87.1.0.12"),sQuery(id+"F30.wireOp",EDGE,"E87.1.0.13"),sQuery(id+"F30.wireOp",EDGE,"E87.1.0.14"),sQuery(id+"F30.wireOp",EDGE,"E87.1.0.15"),sQuery(id+"F30.wireOp",EDGE,"E87.1.0.16"),sQuery(id+"F30.wireOp",EDGE,"E87.1.0.17"),sQuery(id+"F30.wireOp",EDGE,"E87.1.0.18"),sQuery(id+"F30.wireOp",EDGE,"E87.1.0.19"),sQuery(id+"F30.wireOp",EDGE,"E87.1.0.20")])],"isStart":true});
            var Q1;
            Q1=makeQuery(id+"F32.opExtrude","CAP_FACE",FACE,{"disambiguationData":[OSD([sQuery(id+"F30.wireOp",EDGE,"E74.bottom"),sQuery(id+"F30.wireOp",EDGE,"E74.top"),sQuery(id+"F30.wireOp",EDGE,"E74.left"),sQuery(id+"F30.wireOp",EDGE,"E74.right"),sQuery(id+"F30.wireOp",EDGE,"E75.0"),sQuery(id+"F30.wireOp",EDGE,"E75.1"),sQuery(id+"F30.wireOp",EDGE,"E75.2"),sQuery(id+"F30.wireOp",EDGE,"E75.3"),sQuery(id+"F30.wireOp",EDGE,"E76.left"),sQuery(id+"F30.wireOp",EDGE,"E76.right"),sQuery(id+"F30.wireOp",EDGE,"E77.bottom"),sQuery(id+"F30.wireOp",EDGE,"E77.top"),sQuery(id+"F30.wireOp",EDGE,"E78.trimOffspring"),sQuery(id+"F30.wireOp",EDGE,"E79.trimOffspring"),sQuery(id+"F30.wireOp",EDGE,"E80.trimOffspring"),sQuery(id+"F30.wireOp",EDGE,"E81.trimOffspring"),sQuery(id+"F30.wireOp",EDGE,"E82.trimOffspring"),sQuery(id+"F30.wireOp",EDGE,"E83.trimOffspring"),sQuery(id+"F30.wireOp",EDGE,"E84.trimOffspring"),sQuery(id+"F30.wireOp",EDGE,"E85.trimOffspring")])],"isStart":true});
            var Q2;
            Q2=makeQuery(id+"F32.opExtrude","CAP_FACE",FACE,{"disambiguationData":[OSD([sQuery(id+"F30.wireOp",EDGE,"E88.1.0.0"),sQuery(id+"F30.wireOp",EDGE,"E88.1.0.2"),sQuery(id+"F30.wireOp",EDGE,"E88.1.0.3"),sQuery(id+"F30.wireOp",EDGE,"E88.1.0.4"),sQuery(id+"F30.wireOp",EDGE,"E88.1.0.5"),sQuery(id+"F30.wireOp",EDGE,"E88.1.0.6"),sQuery(id+"F30.wireOp",EDGE,"E88.1.0.8"),sQuery(id+"F30.wireOp",EDGE,"E88.1.0.9"),sQuery(id+"F30.wireOp",EDGE,"E88.1.0.10"),sQuery(id+"F30.wireOp",EDGE,"E88.1.0.11"),sQuery(id+"F30.wireOp",EDGE,"E88.1.0.12"),sQuery(id+"F30.wireOp",EDGE,"E88.1.0.13"),sQuery(id+"F30.wireOp",EDGE,"E88.1.0.14"),sQuery(id+"F30.wireOp",EDGE,"E88.1.0.15"),sQuery(id+"F30.wireOp",EDGE,"E88.1.0.16"),sQuery(id+"F30.wireOp",EDGE,"E88.1.0.17"),sQuery(id+"F30.wireOp",EDGE,"E88.1.0.18"),sQuery(id+"F30.wireOp",EDGE,"E88.1.0.19"),sQuery(id+"F30.wireOp",EDGE,"E88.1.0.20"),sQuery(id+"F30.wireOp",EDGE,"E88.1.0.21")])],"isStart":true});
            extrude(context, id + "F35", {"entities" : qUnion([Q0, Q1, Q2]), "operationType" : NewBodyOperationType.REMOVE, "oppositeDirection" : true, "depth" : 0.5 * mm, "offsetDistance" : 25 * mm});
        }
        {
            var Q0;
            Q0=makeQuery(id+"F35.boolean.opBoolean","MERGE",FACE,{"derivedFrom":[makeQuery(id+"F32.opExtrude","CAP_FACE",FACE,{"disambiguationData":[OSD([sQuery(id+"F0.wireOp",EDGE,"E5"),sQuery(id+"F2.wireOp",EDGE,"E12"),sQuery(id+"F2.wireOp",EDGE,"E15"),sQuery(id+"F2.wireOp",EDGE,"E16"),sQuery(id+"F12.wireOp",EDGE,"E30.0"),sQuery(id+"F12.wireOp",EDGE,"E30.1"),sQuery(id+"F12.wireOp",EDGE,"E31")])],"isStart":true}),makeQuery(id+"F35.opExtrude","CAP_FACE",FACE,{"disambiguationData":[OSD([sQuery(id+"F30.wireOp",EDGE,"E74.bottom"),sQuery(id+"F30.wireOp",EDGE,"E74.top"),sQuery(id+"F30.wireOp",EDGE,"E74.left"),sQuery(id+"F30.wireOp",EDGE,"E74.right"),sQuery(id+"F30.wireOp",EDGE,"E75.0"),sQuery(id+"F30.wireOp",EDGE,"E75.1"),sQuery(id+"F30.wireOp",EDGE,"E75.2"),sQuery(id+"F30.wireOp",EDGE,"E75.3"),sQuery(id+"F30.wireOp",EDGE,"E76.left"),sQuery(id+"F30.wireOp",EDGE,"E76.right"),sQuery(id+"F30.wireOp",EDGE,"E77.bottom"),sQuery(id+"F30.wireOp",EDGE,"E77.top"),sQuery(id+"F30.wireOp",EDGE,"E78.trimOffspring"),sQuery(id+"F30.wireOp",EDGE,"E79.trimOffspring"),sQuery(id+"F30.wireOp",EDGE,"E80.trimOffspring"),sQuery(id+"F30.wireOp",EDGE,"E81.trimOffspring"),sQuery(id+"F30.wireOp",EDGE,"E82.trimOffspring"),sQuery(id+"F30.wireOp",EDGE,"E83.trimOffspring"),sQuery(id+"F30.wireOp",EDGE,"E84.trimOffspring"),sQuery(id+"F30.wireOp",EDGE,"E85.trimOffspring")])],"isStart":false}),makeQuery(id+"F35.opExtrude","CAP_FACE",FACE,{"disambiguationData":[OSD([sQuery(id+"F30.wireOp",EDGE,"E87.1.0.0"),sQuery(id+"F30.wireOp",EDGE,"E87.1.0.2"),sQuery(id+"F30.wireOp",EDGE,"E87.1.0.3"),sQuery(id+"F30.wireOp",EDGE,"E87.1.0.4"),sQuery(id+"F30.wireOp",EDGE,"E87.1.0.5"),sQuery(id+"F30.wireOp",EDGE,"E87.1.0.6"),sQuery(id+"F30.wireOp",EDGE,"E87.1.0.7"),sQuery(id+"F30.wireOp",EDGE,"E87.1.0.8"),sQuery(id+"F30.wireOp",EDGE,"E87.1.0.9"),sQuery(id+"F30.wireOp",EDGE,"E87.1.0.10"),sQuery(id+"F30.wireOp",EDGE,"E87.1.0.11"),sQuery(id+"F30.wireOp",EDGE,"E87.1.0.12"),sQuery(id+"F30.wireOp",EDGE,"E87.1.0.13"),sQuery(id+"F30.wireOp",EDGE,"E87.1.0.14"),sQuery(id+"F30.wireOp",EDGE,"E87.1.0.15"),sQuery(id+"F30.wireOp",EDGE,"E87.1.0.16"),sQuery(id+"F30.wireOp",EDGE,"E87.1.0.17"),sQuery(id+"F30.wireOp",EDGE,"E87.1.0.18"),sQuery(id+"F30.wireOp",EDGE,"E87.1.0.19"),sQuery(id+"F30.wireOp",EDGE,"E87.1.0.20")])],"isStart":false}),makeQuery(id+"F35.opExtrude","CAP_FACE",FACE,{"disambiguationData":[OSD([sQuery(id+"F30.wireOp",EDGE,"E88.1.0.0"),sQuery(id+"F30.wireOp",EDGE,"E88.1.0.2"),sQuery(id+"F30.wireOp",EDGE,"E88.1.0.3"),sQuery(id+"F30.wireOp",EDGE,"E88.1.0.4"),sQuery(id+"F30.wireOp",EDGE,"E88.1.0.5"),sQuery(id+"F30.wireOp",EDGE,"E88.1.0.6"),sQuery(id+"F30.wireOp",EDGE,"E88.1.0.8"),sQuery(id+"F30.wireOp",EDGE,"E88.1.0.9"),sQuery(id+"F30.wireOp",EDGE,"E88.1.0.10"),sQuery(id+"F30.wireOp",EDGE,"E88.1.0.11"),sQuery(id+"F30.wireOp",EDGE,"E88.1.0.12"),sQuery(id+"F30.wireOp",EDGE,"E88.1.0.13"),sQuery(id+"F30.wireOp",EDGE,"E88.1.0.14"),sQuery(id+"F30.wireOp",EDGE,"E88.1.0.15"),sQuery(id+"F30.wireOp",EDGE,"E88.1.0.16"),sQuery(id+"F30.wireOp",EDGE,"E88.1.0.17"),sQuery(id+"F30.wireOp",EDGE,"E88.1.0.18"),sQuery(id+"F30.wireOp",EDGE,"E88.1.0.19"),sQuery(id+"F30.wireOp",EDGE,"E88.1.0.20"),sQuery(id+"F30.wireOp",EDGE,"E88.1.0.21")])],"isStart":false})]});
            var sketch = newSketch(context, id + "F36", { "sketchPlane" : qUnion([Q0])});
            skLineSegment(sketch, "E89.bottom", {"start": v(-33, 25.68) * mm, "end": v(62, 25.68) * mm});
            skLineSegment(sketch, "E89.top", {"start": v(-33, 8) * mm, "end": v(62, 8) * mm});
            skLineSegment(sketch, "E89.left", {"start": v(-33, 25.68) * mm, "end": v(-33, 8) * mm});
            skLineSegment(sketch, "E89.right", {"start": v(62, 25.68) * mm, "end": v(62, 8) * mm});
            skSolve(sketch);
        }
        {
            var Q0;
            Q0=makeQuery(id+"F36.imprint","IMPRINT",FACE,{"disambiguationData":[TD([[makeQuery(id+"F36.imprint","IMPRINT",EDGE,{"derivedFrom":sQuery(id+"F36.wireOp",EDGE,"E89.bottom")}),-1.0]])]});
            var Q1;
            Q1=makeQuery(id+"F36.imprint","IMPRINT",FACE,{"disambiguationData":[TD([[makeQuery(id+"F36.imprint","IMPRINT",EDGE,{"derivedFrom":makeQuery(id+"F35.boolean.opBoolean","COPY",EDGE,{"derivedFrom":makeQuery(id+"F35.opExtrude","CAP_EDGE",EDGE,{"disambiguationData":[OSD([sQuery(id+"F30.wireOp",EDGE,"E87.1.0.13")])],"isStart":false})})}),-1.0]])]});
            var Q2;
            Q2=makeQuery(id+"F36.imprint","IMPRINT",FACE,{"disambiguationData":[TD([[makeQuery(id+"F36.imprint","IMPRINT",EDGE,{"derivedFrom":makeQuery(id+"F35.boolean.opBoolean","COPY",EDGE,{"derivedFrom":makeQuery(id+"F35.opExtrude","CAP_EDGE",EDGE,{"disambiguationData":[OSD([sQuery(id+"F30.wireOp",EDGE,"E87.1.0.11")])],"isStart":false})})}),1.0]])]});
            var Q3;
            {var subQ1=makeQuery(id+"F35.boolean.opBoolean","COPY",EDGE,{"derivedFrom":makeQuery(id+"F35.opExtrude","CAP_EDGE",EDGE,{"disambiguationData":[OSD([sQuery(id+"F30.wireOp",EDGE,"E87.1.0.3")])],"isStart":false})});Q3=makeQuery(id+"F36.imprint","IMPRINT",FACE,{"disambiguationData":[TD([[makeQuery(id+"F36.imprint","IMPRINT",EDGE,{"derivedFrom":subQ1}),-1.0]])]});}
            var Q4;
            {var subQ1=makeQuery(id+"F35.boolean.opBoolean","COPY",EDGE,{"derivedFrom":makeQuery(id+"F35.opExtrude","CAP_EDGE",EDGE,{"disambiguationData":[OSD([sQuery(id+"F30.wireOp",EDGE,"E87.1.0.0")])],"isStart":false})});Q4=makeQuery(id+"F36.imprint","IMPRINT",FACE,{"disambiguationData":[TD([[makeQuery(id+"F36.imprint","IMPRINT",EDGE,{"derivedFrom":subQ1}),-1.0]])]});}
            var Q5;
            Q5=makeQuery(id+"F36.imprint","IMPRINT",FACE,{"disambiguationData":[TD([[makeQuery(id+"F36.imprint","IMPRINT",EDGE,{"derivedFrom":makeQuery(id+"F35.boolean.opBoolean","COPY",EDGE,{"derivedFrom":makeQuery(id+"F35.opExtrude","CAP_EDGE",EDGE,{"disambiguationData":[OSD([sQuery(id+"F30.wireOp",EDGE,"E75.3")])],"isStart":false})})}),1.0]])]});
            var Q6;
            Q6=makeQuery(id+"F36.imprint","IMPRINT",FACE,{"disambiguationData":[TD([[makeQuery(id+"F36.imprint","IMPRINT",EDGE,{"derivedFrom":makeQuery(id+"F35.boolean.opBoolean","COPY",EDGE,{"derivedFrom":makeQuery(id+"F35.opExtrude","CAP_EDGE",EDGE,{"disambiguationData":[OSD([sQuery(id+"F30.wireOp",EDGE,"E75.0")])],"isStart":false})})}),1.0]])]});
            var Q7;
            {var subQ1=makeQuery(id+"F35.boolean.opBoolean","COPY",EDGE,{"derivedFrom":makeQuery(id+"F35.opExtrude","CAP_EDGE",EDGE,{"disambiguationData":[OSD([sQuery(id+"F30.wireOp",EDGE,"E79.trimOffspring")])],"isStart":false})});Q7=makeQuery(id+"F36.imprint","IMPRINT",FACE,{"disambiguationData":[TD([[makeQuery(id+"F36.imprint","IMPRINT",EDGE,{"derivedFrom":subQ1}),1.0]])]});}
            var Q8;
            Q8=makeQuery(id+"F36.imprint","IMPRINT",FACE,{"disambiguationData":[TD([[makeQuery(id+"F36.imprint","IMPRINT",EDGE,{"derivedFrom":makeQuery(id+"F35.boolean.opBoolean","COPY",EDGE,{"derivedFrom":makeQuery(id+"F35.opExtrude","CAP_EDGE",EDGE,{"disambiguationData":[OSD([sQuery(id+"F30.wireOp",EDGE,"E77.top")])],"isStart":false})})}),-1.0]])]});
            var Q9;
            Q9=makeQuery(id+"F36.imprint","IMPRINT",FACE,{"disambiguationData":[TD([[makeQuery(id+"F36.imprint","IMPRINT",EDGE,{"derivedFrom":makeQuery(id+"F35.boolean.opBoolean","COPY",EDGE,{"derivedFrom":makeQuery(id+"F35.opExtrude","CAP_EDGE",EDGE,{"disambiguationData":[OSD([sQuery(id+"F30.wireOp",EDGE,"E88.1.0.5")])],"isStart":false})})}),1.0]])]});
            var Q10;
            Q10=makeQuery(id+"F36.imprint","IMPRINT",FACE,{"disambiguationData":[TD([[makeQuery(id+"F36.imprint","IMPRINT",EDGE,{"derivedFrom":makeQuery(id+"F35.boolean.opBoolean","COPY",EDGE,{"derivedFrom":makeQuery(id+"F35.opExtrude","CAP_EDGE",EDGE,{"disambiguationData":[OSD([sQuery(id+"F30.wireOp",EDGE,"E88.1.0.12")])],"isStart":false})})}),1.0]])]});
            var Q11;
            Q11=makeQuery(id+"F36.imprint","IMPRINT",FACE,{"disambiguationData":[TD([[makeQuery(id+"F36.imprint","IMPRINT",EDGE,{"derivedFrom":makeQuery(id+"F35.boolean.opBoolean","COPY",EDGE,{"derivedFrom":makeQuery(id+"F35.opExtrude","CAP_EDGE",EDGE,{"disambiguationData":[OSD([sQuery(id+"F30.wireOp",EDGE,"E88.1.0.9")])],"isStart":false})})}),-1.0]])]});
            var Q12;
            {var subQ1=makeQuery(id+"F35.boolean.opBoolean","COPY",EDGE,{"derivedFrom":makeQuery(id+"F35.opExtrude","CAP_EDGE",EDGE,{"disambiguationData":[OSD([sQuery(id+"F30.wireOp",EDGE,"E88.1.0.8")])],"isStart":false})});Q12=makeQuery(id+"F36.imprint","IMPRINT",FACE,{"disambiguationData":[TD([[makeQuery(id+"F36.imprint","IMPRINT",EDGE,{"derivedFrom":subQ1}),-1.0]])]});}
            extrude(context, id + "F37", {"entities" : qUnion([Q0, Q1, Q2, Q3, Q4, Q5, Q6, Q7, Q8, Q9, Q10, Q11, Q12]), "operationType" : NewBodyOperationType.ADD, "oppositeDirection" : true, "depth" : 24.5 * mm, "offsetDistance" : 25 * mm});
        }
        {
            var Q0;
            Q0=makeQuery(id+"F30.imprint","IMPRINT",FACE,{"disambiguationData":[TD([[makeQuery(id+"F30.imprint","IMPRINT",EDGE,{"derivedFrom":sQuery(id+"F30.wireOp",EDGE,"E87.1.0.13")}),1.0]])]});
            var Q1;
            Q1=makeQuery(id+"F30.imprint","IMPRINT",FACE,{"disambiguationData":[TD([[makeQuery(id+"F30.imprint","IMPRINT",EDGE,{"derivedFrom":sQuery(id+"F30.wireOp",EDGE,"E87.1.0.11")}),-1.0]])]});
            var Q2;
            Q2=makeQuery(id+"F30.imprint","IMPRINT",FACE,{"disambiguationData":[TD([[makeQuery(id+"F30.imprint","IMPRINT",EDGE,{"derivedFrom":sQuery(id+"F30.wireOp",EDGE,"E87.1.0.3")}),1.0]])]});
            var Q3;
            Q3=makeQuery(id+"F30.imprint","IMPRINT",FACE,{"disambiguationData":[TD([[makeQuery(id+"F30.imprint","IMPRINT",EDGE,{"derivedFrom":sQuery(id+"F30.wireOp",EDGE,"E87.1.0.0")}),1.0]])]});
            var Q4;
            Q4=makeQuery(id+"F30.imprint","IMPRINT",FACE,{"disambiguationData":[TD([[makeQuery(id+"F30.imprint","IMPRINT",EDGE,{"derivedFrom":sQuery(id+"F30.wireOp",EDGE,"E75.3")}),-1.0]])]});
            var Q5;
            Q5=makeQuery(id+"F30.imprint","IMPRINT",FACE,{"disambiguationData":[TD([[makeQuery(id+"F30.imprint","IMPRINT",EDGE,{"derivedFrom":sQuery(id+"F30.wireOp",EDGE,"E77.top")}),1.0]])]});
            var Q6;
            Q6=makeQuery(id+"F30.imprint","IMPRINT",FACE,{"disambiguationData":[TD([[makeQuery(id+"F30.imprint","IMPRINT",EDGE,{"derivedFrom":sQuery(id+"F30.wireOp",EDGE,"E75.2")}),1.0]])]});
            var Q7;
            Q7=makeQuery(id+"F30.imprint","IMPRINT",FACE,{"disambiguationData":[TD([[makeQuery(id+"F30.imprint","IMPRINT",EDGE,{"derivedFrom":sQuery(id+"F30.wireOp",EDGE,"E75.0")}),-1.0]])]});
            var Q8;
            Q8=makeQuery(id+"F30.imprint","IMPRINT",FACE,{"disambiguationData":[TD([[makeQuery(id+"F30.imprint","IMPRINT",EDGE,{"derivedFrom":sQuery(id+"F30.wireOp",EDGE,"E88.1.0.5")}),-1.0]])]});
            var Q9;
            Q9=makeQuery(id+"F30.imprint","IMPRINT",FACE,{"disambiguationData":[TD([[makeQuery(id+"F30.imprint","IMPRINT",EDGE,{"derivedFrom":sQuery(id+"F30.wireOp",EDGE,"E88.1.0.12")}),-1.0]])]});
            var Q10;
            Q10=makeQuery(id+"F30.imprint","IMPRINT",FACE,{"disambiguationData":[TD([[makeQuery(id+"F30.imprint","IMPRINT",EDGE,{"derivedFrom":sQuery(id+"F30.wireOp",EDGE,"E88.1.0.6")}),1.0]])]});
            var Q11;
            Q11=makeQuery(id+"F30.imprint","IMPRINT",FACE,{"disambiguationData":[TD([[makeQuery(id+"F30.imprint","IMPRINT",EDGE,{"derivedFrom":sQuery(id+"F30.wireOp",EDGE,"E88.1.0.0")}),1.0]])]});
            extrude(context, id + "F38", {"entities" : qUnion([Q0, Q1, Q2, Q3, Q4, Q5, Q6, Q7, Q8, Q9, Q10, Q11]), "operationType" : NewBodyOperationType.ADD, "depth" : 25 * mm, "offsetDistance" : 25 * mm});
        }
        {
            var Q0;
            Q0=makeQuery(id+"F38.opExtrude","SWEPT_FACE",FACE,{"disambiguationData":[OSD([sQuery(id+"F30.wireOp",EDGE,"E88.1.0.6")])]});
            var Q1;
            Q1=makeQuery(id+"F38.opExtrude","SWEPT_FACE",FACE,{"disambiguationData":[OSD([sQuery(id+"F30.wireOp",EDGE,"E88.1.0.0")])]});
            var Q2;
            Q2=makeQuery(id+"F38.opExtrude","SWEPT_FACE",FACE,{"disambiguationData":[OSD([sQuery(id+"F30.wireOp",EDGE,"E75.2")])]});
            var Q3;
            Q3=makeQuery(id+"F38.opExtrude","SWEPT_FACE",FACE,{"disambiguationData":[OSD([sQuery(id+"F30.wireOp",EDGE,"E85.trimOffspring")])]});
            var Q4;
            Q4=makeQuery(id+"F38.opExtrude","SWEPT_FACE",FACE,{"disambiguationData":[OSD([sQuery(id+"F30.wireOp",EDGE,"E87.1.0.14")])]});
            var Q5;
            Q5=makeQuery(id+"F38.opExtrude","SWEPT_FACE",FACE,{"disambiguationData":[OSD([sQuery(id+"F30.wireOp",EDGE,"E87.1.0.2")])]});
            extrude(context, id + "F39", {"entities" : qUnion([Q0, Q1, Q2, Q3, Q4, Q5]), "operationType" : NewBodyOperationType.REMOVE, "oppositeDirection" : true, "depth" : 1.05 * mm, "offsetDistance" : 25 * mm});
        }
    });
